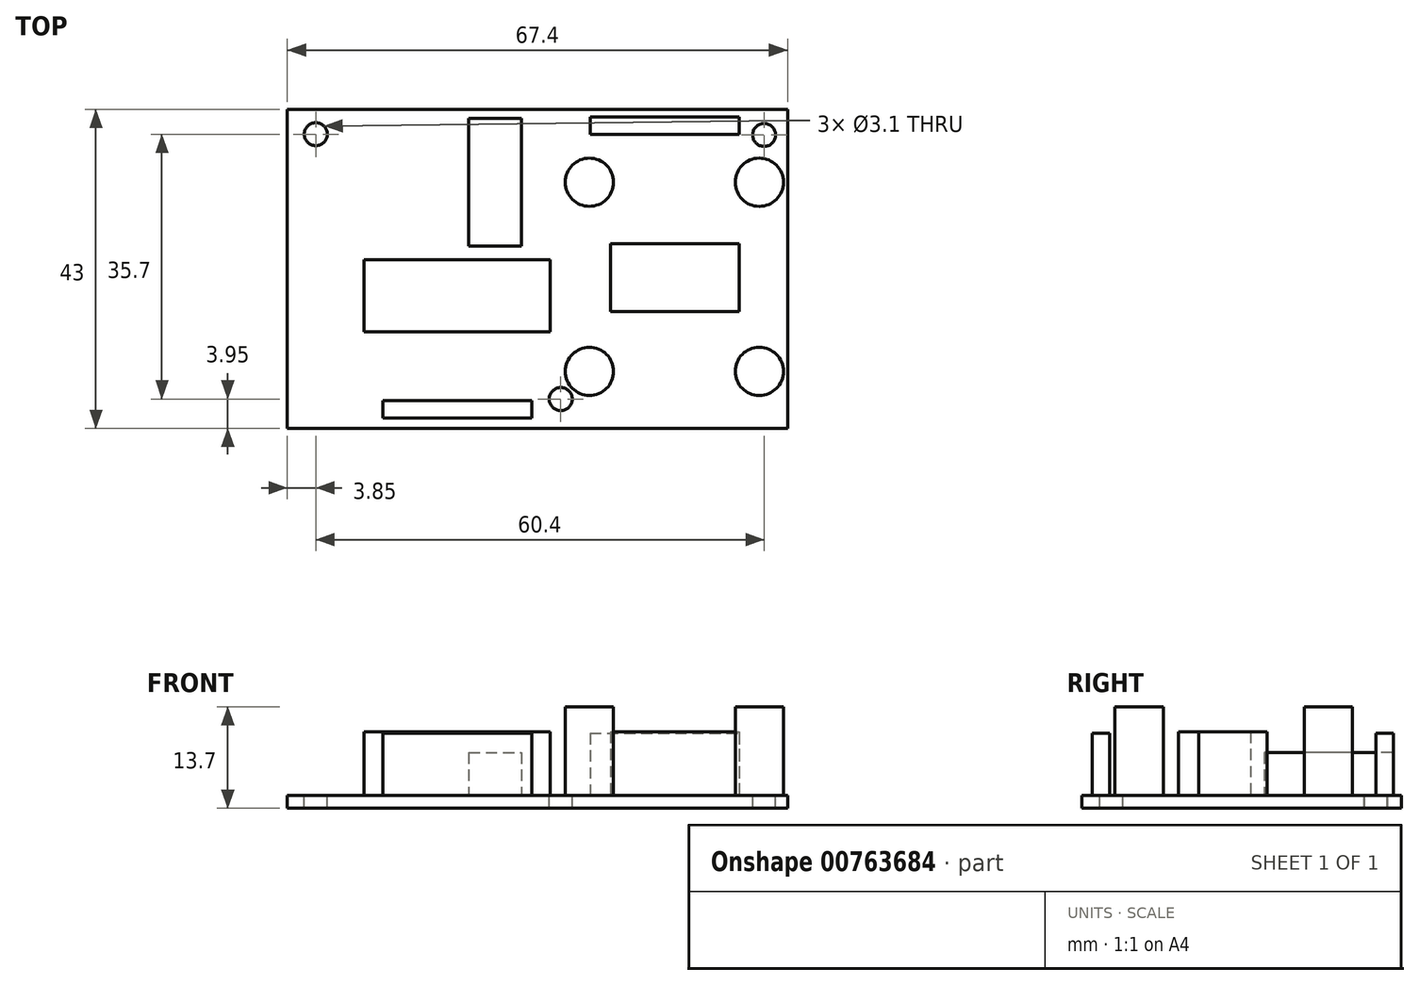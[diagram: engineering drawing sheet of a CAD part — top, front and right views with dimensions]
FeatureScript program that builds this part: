
annotation { "Feature Type Name" : "Feature", "Feature Type Description" : "" }
export const myFeature = defineFeature(function(context is Context, id is Id, definition is map)
    precondition{}
    {
        {
            var Q0;
            Q0=qCreatedBy(makeId("Top.planeOp"),FACE);
            var sketch = newSketch(context, id + "F0", { "sketchPlane" : qUnion([Q0])});
            skLineSegment(sketch, "E0.bottom", {"start": v(33.7, 21.5) * mm, "end": v(-33.7, 21.5) * mm});
            skLineSegment(sketch, "E0.top", {"start": v(33.7, -21.5) * mm, "end": v(-33.7, -21.5) * mm});
            skLineSegment(sketch, "E0.left", {"start": v(33.7, 21.5) * mm, "end": v(33.7, -21.5) * mm});
            skLineSegment(sketch, "E0.right", {"start": v(-33.7, 21.5) * mm, "end": v(-33.7, -21.5) * mm});
            skPoint(sketch, "E0.middle", {"position": v(0, 0) * mm});
            skSolve(sketch);
        }
        {
            var Q0;
            Q0=makeQuery(id+"F0.imprint","IMPRINT",FACE,{"disambiguationData":[TD([[makeQuery(id+"F0.imprint","IMPRINT",EDGE,{"derivedFrom":sQuery(id+"F0.wireOp",EDGE,"E0.bottom")}),1.0]])]});
            extrude(context, id + "F1", {"entities" : qUnion([Q0]), "depth" : 1.7 * mm, "offsetDistance" : 25 * mm});
        }
        {
            var Q0;
            Q0=makeQuery(id+"F1.opExtrude","CAP_FACE",FACE,{"disambiguationData":[OSD([sQuery(id+"F0.wireOp",EDGE,"E0.bottom"),sQuery(id+"F0.wireOp",EDGE,"E0.top"),sQuery(id+"F0.wireOp",EDGE,"E0.left"),sQuery(id+"F0.wireOp",EDGE,"E0.right")])],"isStart":false});
            var sketch = newSketch(context, id + "F2", { "sketchPlane" : qUnion([Q0])});
            skCircle(sketch, "E1", {"center": v(-29.85, 18.15) * mm, "radius": 1.55 * mm});
            skCircle(sketch, "E2", {"center": v(3.15, -17.55) * mm, "radius": 1.55 * mm});
            skCircle(sketch, "E3", {"center": v(30.55, 18.05) * mm, "radius": 1.55 * mm});
            skSolve(sketch);
        }
        {
            var Q0;
            Q0=makeQuery(id+"F2.imprint","IMPRINT",FACE,{"disambiguationData":[TD([[makeQuery(id+"F2.imprint","IMPRINT",EDGE,{"derivedFrom":sQuery(id+"F2.wireOp",EDGE,"E1")}),1.0]])]});
            var Q1;
            Q1=makeQuery(id+"F2.imprint","IMPRINT",FACE,{"disambiguationData":[TD([[makeQuery(id+"F2.imprint","IMPRINT",EDGE,{"derivedFrom":sQuery(id+"F2.wireOp",EDGE,"E2")}),1.0]])]});
            var Q2;
            Q2=makeQuery(id+"F2.imprint","IMPRINT",FACE,{"disambiguationData":[TD([[makeQuery(id+"F2.imprint","IMPRINT",EDGE,{"derivedFrom":sQuery(id+"F2.wireOp",EDGE,"E3")}),1.0]])]});
            extrude(context, id + "F3", {"entities" : qUnion([Q0, Q1, Q2]), "operationType" : NewBodyOperationType.REMOVE, "oppositeDirection" : true, "depth" : 25 * mm, "offsetDistance" : 25 * mm});
        }
        {
            var Q0;
            Q0=makeQuery(id+"F1.opExtrude","CAP_FACE",FACE,{"disambiguationData":[OSD([sQuery(id+"F0.wireOp",EDGE,"E0.bottom"),sQuery(id+"F0.wireOp",EDGE,"E0.top"),sQuery(id+"F0.wireOp",EDGE,"E0.left"),sQuery(id+"F0.wireOp",EDGE,"E0.right")])],"isStart":false});
            var sketch = newSketch(context, id + "F4", { "sketchPlane" : qUnion([Q0])});
            skLineSegment(sketch, "E4.bottom", {"start": v(-20.84, -17.76) * mm, "end": v(-0.75, -17.76) * mm});
            skLineSegment(sketch, "E4.top", {"start": v(-20.84, -20.12) * mm, "end": v(-0.75, -20.12) * mm});
            skLineSegment(sketch, "E4.left", {"start": v(-20.84, -17.76) * mm, "end": v(-20.84, -20.12) * mm});
            skLineSegment(sketch, "E4.right", {"start": v(-0.75, -17.76) * mm, "end": v(-0.75, -20.12) * mm});
            skLineSegment(sketch, "E5.bottom", {"start": v(7.1, 20.45) * mm, "end": v(27.18, 20.45) * mm});
            skLineSegment(sketch, "E5.top", {"start": v(7.1, 18.1) * mm, "end": v(27.18, 18.1) * mm});
            skLineSegment(sketch, "E5.left", {"start": v(7.1, 20.45) * mm, "end": v(7.1, 18.1) * mm});
            skLineSegment(sketch, "E5.right", {"start": v(27.18, 20.45) * mm, "end": v(27.18, 18.1) * mm});
            skLineSegment(sketch, "E6.bottom", {"start": v(-23.35, -8.5) * mm, "end": v(1.76, -8.5) * mm});
            skLineSegment(sketch, "E6.top", {"start": v(-23.35, 1.22) * mm, "end": v(1.76, 1.22) * mm});
            skLineSegment(sketch, "E6.left", {"start": v(-23.35, -8.5) * mm, "end": v(-23.35, 1.22) * mm});
            skLineSegment(sketch, "E6.right", {"start": v(1.76, -8.5) * mm, "end": v(1.76, 1.22) * mm});
            skLineSegment(sketch, "E7.bottom", {"start": v(9.84, -5.76) * mm, "end": v(27.18, -5.76) * mm});
            skLineSegment(sketch, "E7.top", {"start": v(9.84, 3.42) * mm, "end": v(27.18, 3.42) * mm});
            skLineSegment(sketch, "E7.left", {"start": v(9.84, -5.76) * mm, "end": v(9.84, 3.42) * mm});
            skLineSegment(sketch, "E7.right", {"start": v(27.18, -5.76) * mm, "end": v(27.18, 3.42) * mm});
            skLineSegment(sketch, "E8.bottom", {"start": v(-9.23, 20.29) * mm, "end": v(-2.17, 20.29) * mm});
            skLineSegment(sketch, "E8.top", {"start": v(-9.23, 3.06) * mm, "end": v(-2.17, 3.06) * mm});
            skLineSegment(sketch, "E8.left", {"start": v(-9.23, 20.29) * mm, "end": v(-9.23, 3.06) * mm});
            skLineSegment(sketch, "E8.right", {"start": v(-2.17, 20.29) * mm, "end": v(-2.17, 3.06) * mm});
            skCircle(sketch, "E9", {"center": v(7, 11.67) * mm, "radius": 3.25 * mm});
            skPoint(sketch, "E9.centerSnap0", {"position": v(-2.17, 11.67) * mm});
            skCircle(sketch, "E10", {"center": v(29.9, 11.67) * mm, "radius": 3.25 * mm});
            skCircle(sketch, "E11", {"center": v(7, -13.82) * mm, "radius": 3.25 * mm});
            skCircle(sketch, "E12", {"center": v(29.9, -13.82) * mm, "radius": 3.25 * mm});
            skSolve(sketch);
        }
        {
            var Q0;
            Q0=makeQuery(id+"F4.imprint","IMPRINT",FACE,{"disambiguationData":[TD([[makeQuery(id+"F4.imprint","IMPRINT",EDGE,{"derivedFrom":sQuery(id+"F4.wireOp",EDGE,"E6.bottom")}),1.0]])]});
            var Q1;
            Q1=makeQuery(id+"F4.imprint","IMPRINT",FACE,{"disambiguationData":[TD([[makeQuery(id+"F4.imprint","IMPRINT",EDGE,{"derivedFrom":sQuery(id+"F4.wireOp",EDGE,"E7.bottom")}),1.0]])]});
            extrude(context, id + "F5", {"entities" : qUnion([Q0, Q1]), "operationType" : NewBodyOperationType.ADD, "depth" : 8.6 * mm, "offsetDistance" : 25 * mm});
        }
        {
            var Q0;
            Q0=makeQuery(id+"F4.imprint","IMPRINT",FACE,{"disambiguationData":[TD([[makeQuery(id+"F4.imprint","IMPRINT",EDGE,{"derivedFrom":sQuery(id+"F4.wireOp",EDGE,"E11")}),1.0]])]});
            var Q1;
            Q1=makeQuery(id+"F4.imprint","IMPRINT",FACE,{"disambiguationData":[TD([[makeQuery(id+"F4.imprint","IMPRINT",EDGE,{"derivedFrom":sQuery(id+"F4.wireOp",EDGE,"E9")}),1.0]])]});
            var Q2;
            Q2=makeQuery(id+"F4.imprint","IMPRINT",FACE,{"disambiguationData":[TD([[makeQuery(id+"F4.imprint","IMPRINT",EDGE,{"derivedFrom":sQuery(id+"F4.wireOp",EDGE,"E10")}),1.0]])]});
            var Q3;
            Q3=makeQuery(id+"F4.imprint","IMPRINT",FACE,{"disambiguationData":[TD([[makeQuery(id+"F4.imprint","IMPRINT",EDGE,{"derivedFrom":sQuery(id+"F4.wireOp",EDGE,"E12")}),1.0]])]});
            extrude(context, id + "F6", {"entities" : qUnion([Q0, Q1, Q2, Q3]), "operationType" : NewBodyOperationType.ADD, "depth" : 12 * mm, "offsetDistance" : 25 * mm});
        }
        {
            var Q0;
            Q0=makeQuery(id+"F4.imprint","IMPRINT",FACE,{"disambiguationData":[TD([[makeQuery(id+"F4.imprint","IMPRINT",EDGE,{"derivedFrom":sQuery(id+"F4.wireOp",EDGE,"E4.bottom")}),-1.0]])]});
            var Q1;
            Q1=makeQuery(id+"F4.imprint","IMPRINT",FACE,{"disambiguationData":[TD([[makeQuery(id+"F4.imprint","IMPRINT",EDGE,{"derivedFrom":sQuery(id+"F4.wireOp",EDGE,"E5.bottom")}),-1.0]])]});
            extrude(context, id + "F7", {"entities" : qUnion([Q0, Q1]), "operationType" : NewBodyOperationType.ADD, "depth" : 8.4 * mm, "offsetDistance" : 25 * mm});
        }
        {
            var Q0;
            Q0=makeQuery(id+"F4.imprint","IMPRINT",FACE,{"disambiguationData":[TD([[makeQuery(id+"F4.imprint","IMPRINT",EDGE,{"derivedFrom":sQuery(id+"F4.wireOp",EDGE,"E8.bottom")}),-1.0]])]});
            extrude(context, id + "F8", {"entities" : qUnion([Q0]), "operationType" : NewBodyOperationType.ADD, "depth" : 5.8 * mm, "offsetDistance" : 25 * mm});
        }
    });
